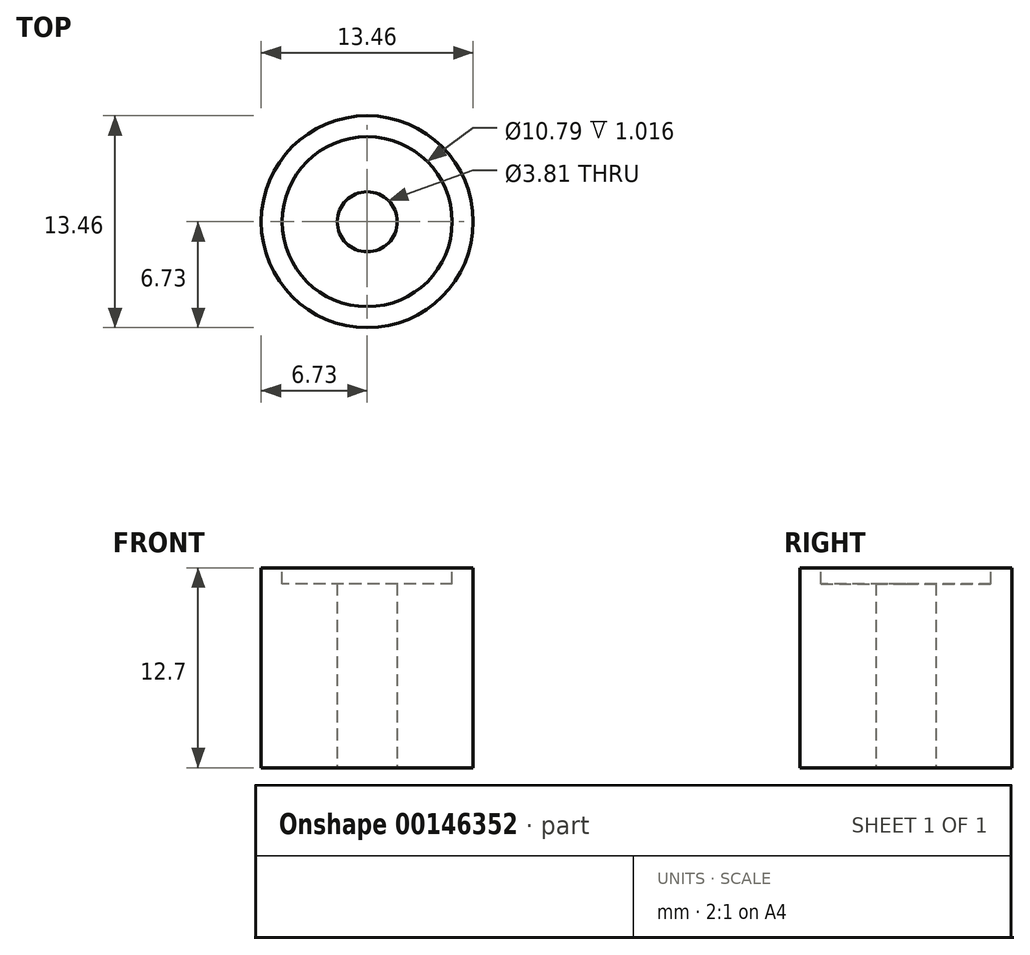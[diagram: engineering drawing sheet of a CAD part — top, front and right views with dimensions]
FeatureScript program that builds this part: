
annotation { "Feature Type Name" : "Feature", "Feature Type Description" : "" }
export const myFeature = defineFeature(function(context is Context, id is Id, definition is map)
    precondition{}
    {
        {
            var Q0;
            Q0=qCreatedBy(makeId("Top.planeOp"),FACE);
            var sketch = newSketch(context, id + "F0", { "sketchPlane" : qUnion([Q0])});
            skCircle(sketch, "E0", {"center": v(0, 0) * mm, "radius": 6.73 * mm});
            skSolve(sketch);
        }
        {
            var Q0;
            Q0 = qSketchRegion(id + "F0", true);
            extrude(context, id + "F1", {"entities" : qUnion([Q0]), "depth" : 12.7 * mm});
        }
        {
            var Q0;
            Q0=makeQuery(id+"F1.opExtrude","CAP_FACE",FACE,{"disambiguationData":[OSD([sQuery(id+"F0.wireOp",EDGE,"E0")])],"isStart":false});
            var sketch = newSketch(context, id + "F2", { "sketchPlane" : qUnion([Q0])});
            skCircle(sketch, "E1", {"center": v(0, 0) * mm, "radius": 5.4 * mm});
            skSolve(sketch);
        }
        {
            var Q0;
            Q0 = qSketchRegion(id + "F2", true);
            extrude(context, id + "F3", {"entities" : qUnion([Q0]), "operationType" : NewBodyOperationType.REMOVE, "oppositeDirection" : true, "depth" : 1.02 * mm});
        }
        {
            var Q0;
            Q0=makeQuery(id+"F1.opExtrude","CAP_FACE",FACE,{"disambiguationData":[OSD([sQuery(id+"F0.wireOp",EDGE,"E0")])],"isStart":true});
            var sketch = newSketch(context, id + "F4", { "sketchPlane" : qUnion([Q0])});
            skCircle(sketch, "E2", {"center": v(0, 0) * mm, "radius": 1.9 * mm});
            skSolve(sketch);
        }
        {
            var Q0;
            Q0 = qSketchRegion(id + "F4", true);
            extrude(context, id + "F5", {"entities" : qUnion([Q0]), "operationType" : NewBodyOperationType.REMOVE, "oppositeDirection" : true, "depth" : 25.4 * mm});
        }
    });
